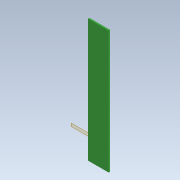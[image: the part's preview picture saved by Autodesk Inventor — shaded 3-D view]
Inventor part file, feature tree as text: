
AUTODESK INVENTOR PART (.ipt)
format: ipt  version: 2021 (Build 250183000, 183)  size: 77,312 bytes
history: native  units: in
note: dims shown in document units (in); Inventor stores cm internally (conversion verified against a paired STEP export)
features: other x2, plane x1, extrude x1, sketch x1
ambient origin geometry x8: Origin, YZ Plane, XZ Plane, XY Plane, X Axis, Y Axis, Z Axis, Center Point
bodies: Solid1 (feature_tree)
feature tree (5):
  plane  "Work Plane1"
  extrude  "Extrusion1"  Depth=5.3488in
  sketch  "Sketch1"  dims[d0=0.9in d1=5.3488in d2=0.064in d3=0.0in]
  other  "Tractive Light Assembly.iam"
  other  "Tractive Light Mount:1"
